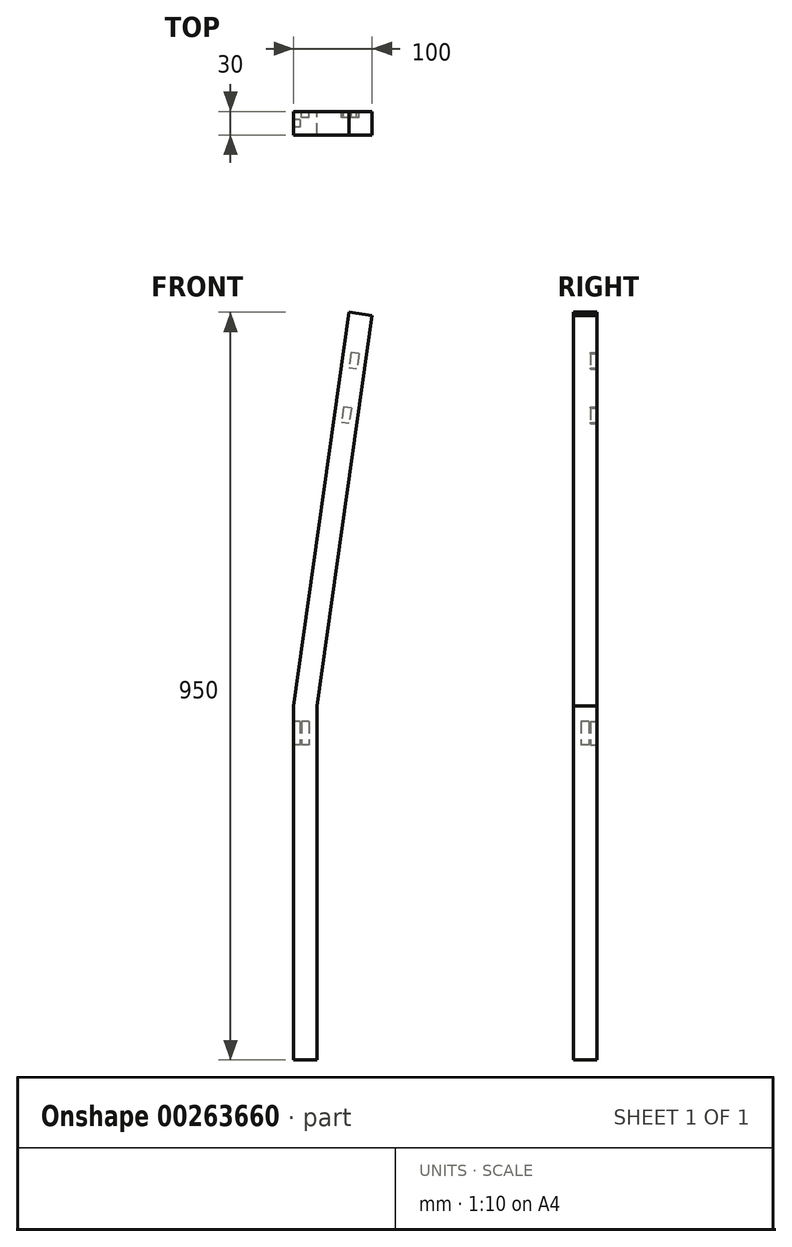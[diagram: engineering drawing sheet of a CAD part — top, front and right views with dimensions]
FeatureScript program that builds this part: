
annotation { "Feature Type Name" : "Feature", "Feature Type Description" : "" }
export const myFeature = defineFeature(function(context is Context, id is Id, definition is map)
    precondition{}
    {
        {
            var Q0;
            Q0=qCreatedBy(makeId("Front.planeOp"),FACE);
            var sketch = newSketch(context, id + "F0", { "sketchPlane" : qUnion([Q0])});
            skLineSegment(sketch, "E0", {"start": v(0, 0) * mm, "end": v(0, -450) * mm});
            skLineSegment(sketch, "E1", {"start": v(0, -450) * mm, "end": v(30, -450) * mm});
            skLineSegment(sketch, "E2", {"start": v(30, -450) * mm, "end": v(30, 0) * mm});
            skLineSegment(sketch, "E3", {"start": v(30, 0) * mm, "end": v(100, 495.8) * mm});
            skLineSegment(sketch, "E4", {"start": v(100, 495.8) * mm, "end": v(70.3, 500) * mm});
            skLineSegment(sketch, "E5", {"start": v(70.3, 500) * mm, "end": v(0, 0) * mm});
            skSolve(sketch);
        }
        {
            var Q0;
            Q0=qSketchRegion(id+"F0",true);
            extrude(context, id + "F1", {"entities" : qUnion([Q0]), "depth" : 30 * mm});
        }
        {
            var Q0;
            Q0=makeQuery(id+"F1.opExtrude","CAP_FACE",FACE,{"disambiguationData":[OSD([sQuery(id+"F0.wireOp",EDGE,"E0"),sQuery(id+"F0.wireOp",EDGE,"E1"),sQuery(id+"F0.wireOp",EDGE,"E2"),sQuery(id+"F0.wireOp",EDGE,"E3"),sQuery(id+"F0.wireOp",EDGE,"E4"),sQuery(id+"F0.wireOp",EDGE,"E5")])],"isStart":true});
            var sketch = newSketch(context, id + "F2", { "sketchPlane" : qUnion([Q0])});
            skLineSegment(sketch, "E6.bottom", {"start": v(-83.14, 447.7) * mm, "end": v(-73.23, 449.09) * mm});
            skLineSegment(sketch, "E6.top", {"start": v(-80.35, 427.89) * mm, "end": v(-70.45, 429.28) * mm});
            skLineSegment(sketch, "E6.left", {"start": v(-83.14, 447.7) * mm, "end": v(-80.35, 427.89) * mm});
            skLineSegment(sketch, "E6.right", {"start": v(-73.23, 449.09) * mm, "end": v(-70.45, 429.28) * mm});
            skLineSegment(sketch, "E7.bottom", {"start": v(-73.4, 378.38) * mm, "end": v(-63.49, 379.77) * mm});
            skLineSegment(sketch, "E7.top", {"start": v(-70.6, 358.57) * mm, "end": v(-60.7, 359.96) * mm});
            skLineSegment(sketch, "E7.left", {"start": v(-73.4, 378.38) * mm, "end": v(-70.6, 358.57) * mm});
            skLineSegment(sketch, "E7.right", {"start": v(-63.49, 379.77) * mm, "end": v(-60.7, 359.96) * mm});
            skSolve(sketch);
        }
        {
            var Q0;
            Q0=qSketchRegion(id+"F2",true);
            extrude(context, id + "F3", {"entities" : qUnion([Q0]), "operationType" : NewBodyOperationType.REMOVE, "oppositeDirection" : true, "depth" : 8 * mm});
        }
        {
            var Q0;
            Q0=makeQuery(id+"F1.opExtrude","CAP_FACE",FACE,{"disambiguationData":[OSD([sQuery(id+"F0.wireOp",EDGE,"E0"),sQuery(id+"F0.wireOp",EDGE,"E1"),sQuery(id+"F0.wireOp",EDGE,"E2"),sQuery(id+"F0.wireOp",EDGE,"E3"),sQuery(id+"F0.wireOp",EDGE,"E4"),sQuery(id+"F0.wireOp",EDGE,"E5")])],"isStart":true});
            var sketch = newSketch(context, id + "F4", { "sketchPlane" : qUnion([Q0])});
            skLineSegment(sketch, "E8.bottom", {"start": v(-20, -20) * mm, "end": v(-10, -20) * mm});
            skLineSegment(sketch, "E8.top", {"start": v(-20, -50) * mm, "end": v(-10, -50) * mm});
            skLineSegment(sketch, "E8.left", {"start": v(-20, -20) * mm, "end": v(-20, -50) * mm});
            skLineSegment(sketch, "E8.right", {"start": v(-10, -20) * mm, "end": v(-10, -50) * mm});
            skSolve(sketch);
        }
        {
            var Q0;
            Q0=qSketchRegion(id+"F4",true);
            extrude(context, id + "F5", {"entities" : qUnion([Q0]), "operationType" : NewBodyOperationType.REMOVE, "oppositeDirection" : true, "depth" : 8 * mm});
        }
        {
            var Q0;
            Q0=makeQuery(id+"F1.opExtrude","SWEPT_FACE",FACE,{"disambiguationData":[OSD([sQuery(id+"F0.wireOp",EDGE,"E0")])]});
            var sketch = newSketch(context, id + "F6", { "sketchPlane" : qUnion([Q0])});
            skLineSegment(sketch, "E9.bottom", {"start": v(10, -20) * mm, "end": v(20, -20) * mm});
            skLineSegment(sketch, "E9.top", {"start": v(10, -50) * mm, "end": v(20, -50) * mm});
            skLineSegment(sketch, "E9.left", {"start": v(10, -20) * mm, "end": v(10, -50) * mm});
            skLineSegment(sketch, "E9.right", {"start": v(20, -20) * mm, "end": v(20, -50) * mm});
            skSolve(sketch);
        }
        {
            var Q0;
            Q0=qSketchRegion(id+"F6",true);
            extrude(context, id + "F7", {"entities" : qUnion([Q0]), "operationType" : NewBodyOperationType.REMOVE, "oppositeDirection" : true, "depth" : 8 * mm});
        }
    });
